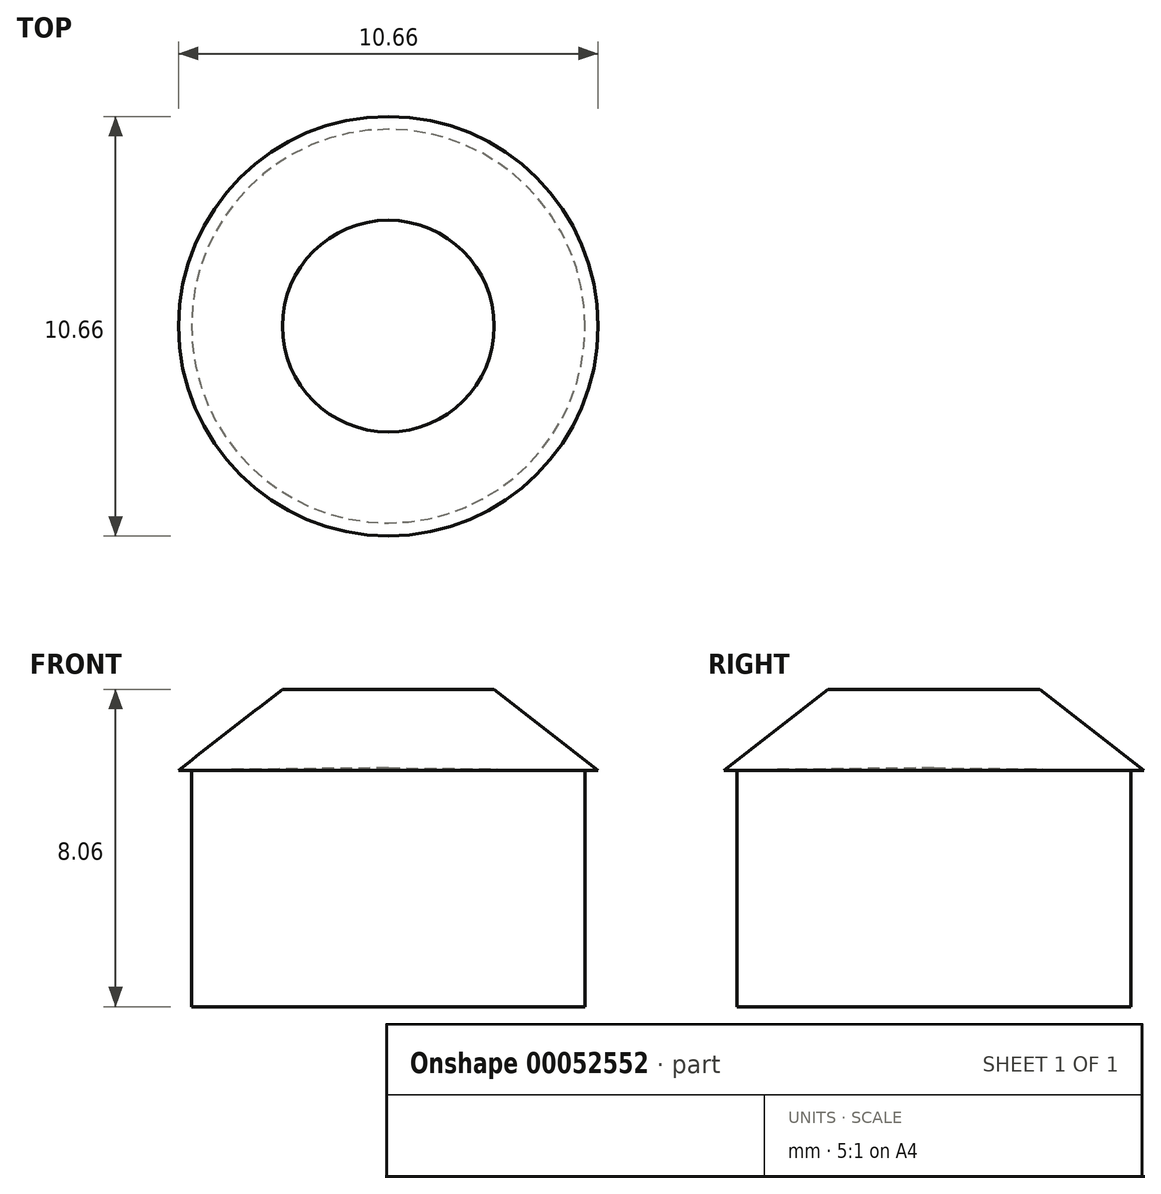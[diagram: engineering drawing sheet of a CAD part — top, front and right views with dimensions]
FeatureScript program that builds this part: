
annotation { "Feature Type Name" : "Feature", "Feature Type Description" : "" }
export const myFeature = defineFeature(function(context is Context, id is Id, definition is map)
    precondition{}
    {
        {
            var Q0;
            Q0=qCreatedBy(makeId("Top.planeOp"),FACE);
            var sketch = newSketch(context, id + "F0", { "sketchPlane" : qUnion([Q0])});
            skCircle(sketch, "E0", {"center": v(0, 0) * mm, "radius": 5 * mm});
            skSolve(sketch);
        }
        {
            var Q0;
            Q0=makeQuery(id+"F0.imprint","IMPRINT",FACE,{"disambiguationData":[TD([[makeQuery(id+"F0.imprint","IMPRINT",EDGE,{"derivedFrom":sQuery(id+"F0.wireOp",EDGE,"E0")}),1.0]])]});
            extrude(context, id + "F1", {"entities" : qUnion([Q0]), "depth" : 6 * mm});
        }
        {
            var Q0;
            Q0=qCreatedBy(makeId("Front.planeOp"),FACE);
            var sketch = newSketch(context, id + "F3", { "sketchPlane" : qUnion([Q0])});
            skLineSegment(sketch, "E1", {"start": v(0, 8.06) * mm, "end": v(0, 8.06) * mm});
            skLineSegment(sketch, "E2", {"start": v(0, 6.06) * mm, "end": v(0, 8.06) * mm});
            skLineSegment(sketch, "E3", {"start": v(0, 8.06) * mm, "end": v(2.7, 8.06) * mm});
            skLineSegment(sketch, "E4", {"start": v(2.7, 8.06) * mm, "end": v(2.7, 8.06) * mm});
            skLineSegment(sketch, "E5", {"start": v(5.33, 6) * mm, "end": v(5.33, 6) * mm});
            skLineSegment(sketch, "E6", {"start": v(2.7, 8.06) * mm, "end": v(5.33, 6) * mm});
            skPoint(sketch, "E7.start.orphan", {"position": v(0, 6) * mm});
            skLineSegment(sketch, "E8", {"start": v(0, 6.06) * mm, "end": v(5.33, 6) * mm});
            skSolve(sketch);
        }
        {
            var Q0;
            Q0 = qSketchRegion(id + "F3", true);
            var Q1;
            Q1=sQuery(id+"F3.wireOp",EDGE,"E2");
            revolve(context, id + "F2", {"entities" : qUnion([Q0]), "axis" : qUnion([Q1]), "revolveType" : RevolveType.FULL});
        }
    });
